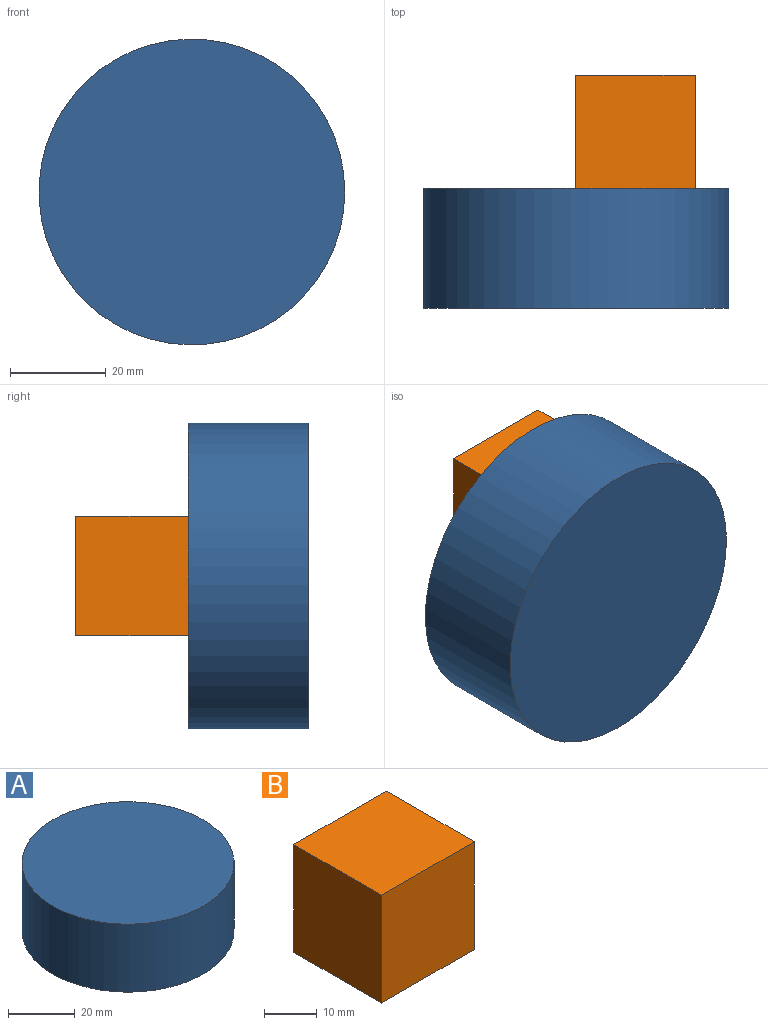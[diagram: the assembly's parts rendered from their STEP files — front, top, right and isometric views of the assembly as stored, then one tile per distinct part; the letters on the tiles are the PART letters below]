
ASSEMBLY  parts=2 mates=1
PART A: 3 faces, bbox 63.7x63.7x25 mm
  f0: cylinder r=31.86mm len=63.72mm, axis (0,0,-1), area 5004.9mm2, adj f1,f2
  f1: plane 63.72x63.72mm, normal (0,0,1), area 3189.3mm2, adj f0
  f2: plane 63.72x63.72mm, normal (0,0,-1), area 3189.3mm2, adj f0
PART B: 6 faces, bbox 24.8x23.5x25 mm
  f0: plane 25x23.52mm, normal (-1,0,0), area 588mm2, adj f1,f3,f4,f5
  f1: plane 25x24.84mm, normal (0,-1,0), area 621mm2, adj f0,f2,f4,f5
  f2: plane 25x23.52mm, normal (1,0,0), area 588mm2, adj f1,f3,f4,f5
  f3: plane 25x24.84mm, normal (0,1,0), area 621mm2, adj f0,f2,f4,f5
  f4: plane 24.84x23.52mm, normal (0,0,1), area 584.2mm2, adj f0,f1,f2,f3
  f5: plane 24.84x23.52mm, normal (0,0,-1), area 584.2mm2, adj f0,f1,f2,f3
PLACE A rot(axis=(-1,0,0),90deg) t=(20.34,-1.74,72.2)mm
PLACE B t=(49.67,-4.36,30.76)mm
MATE parallel A.f0 <-> B.f1  axis (0,1,0) through (-1.72,23.26,43.26)mm
